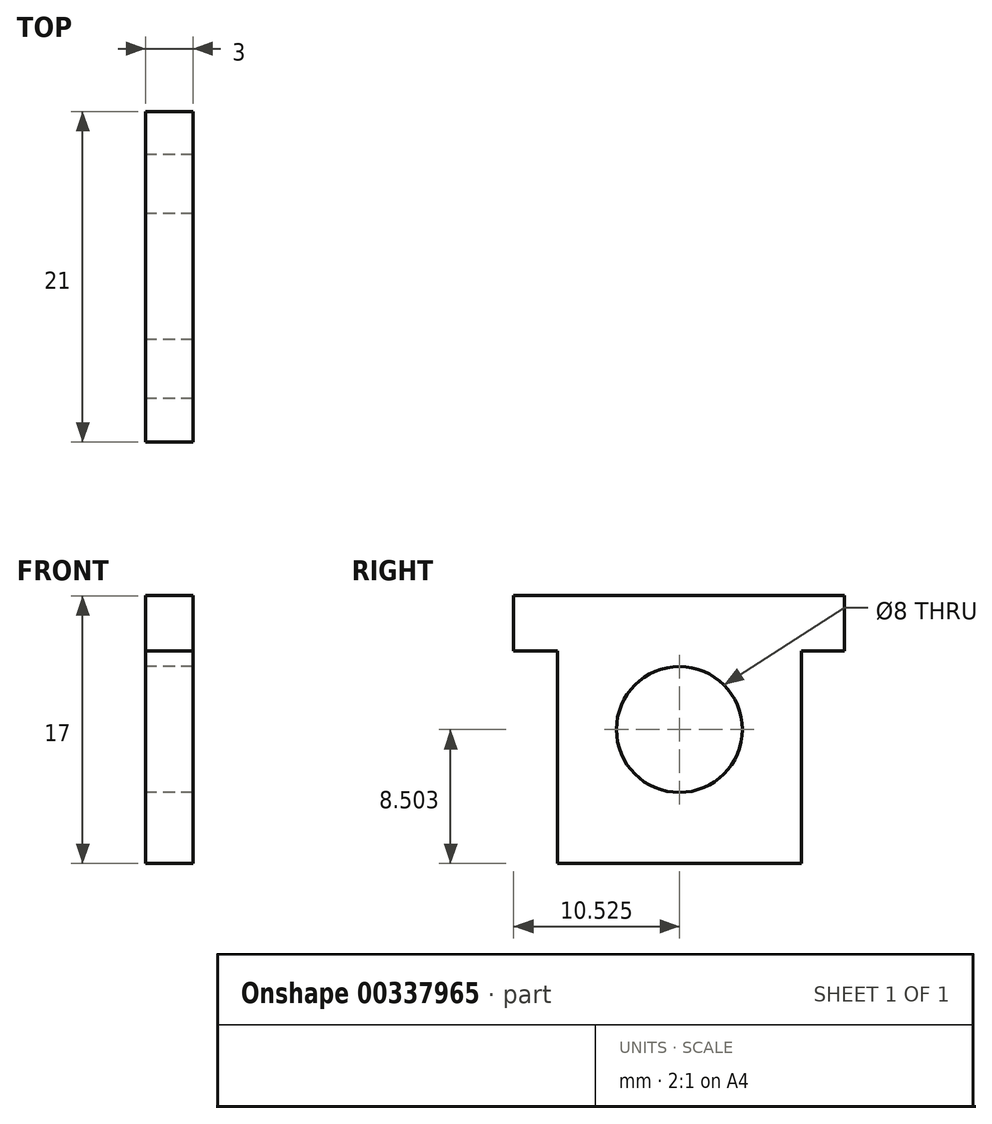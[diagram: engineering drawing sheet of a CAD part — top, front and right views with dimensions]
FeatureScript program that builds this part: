
annotation { "Feature Type Name" : "Feature", "Feature Type Description" : "" }
export const myFeature = defineFeature(function(context is Context, id is Id, definition is map)
    precondition{}
    {
        {
            var Q0;
            Q0=qCreatedBy(makeId("Right.planeOp"),FACE);
            var sketch = newSketch(context, id + "F0", { "sketchPlane" : qUnion([Q0])});
            skLineSegment(sketch, "E0.bottom", {"start": v(-310.36, 146.13) * mm, "end": v(-294.86, 146.13) * mm});
            skLineSegment(sketch, "E0.top", {"start": v(-310.36, 132.63) * mm, "end": v(-294.86, 132.63) * mm});
            skLineSegment(sketch, "E0.left", {"start": v(-310.36, 146.13) * mm, "end": v(-310.36, 132.63) * mm});
            skLineSegment(sketch, "E0.right", {"start": v(-294.86, 146.13) * mm, "end": v(-294.86, 132.63) * mm});
            skPoint(sketch, "E1.oppositeSnap0", {"position": v(-302.6, 146.13) * mm});
            skLineSegment(sketch, "E1.bottom", {"start": v(-313.13, 149.63) * mm, "end": v(-292.13, 149.63) * mm});
            skLineSegment(sketch, "E1.top", {"start": v(-313.13, 146.13) * mm, "end": v(-292.13, 146.13) * mm});
            skLineSegment(sketch, "E1.left", {"start": v(-313.13, 149.63) * mm, "end": v(-313.13, 146.13) * mm});
            skLineSegment(sketch, "E1.right", {"start": v(-292.13, 149.63) * mm, "end": v(-292.13, 146.13) * mm});
            skCircle(sketch, "E2", {"center": v(-302.6, 141.13) * mm, "radius": 4 * mm});
            skSolve(sketch);
        }
        {
            var Q0;
            Q0 = qSketchRegion(id + "F0", true);
            extrude(context, id + "F1", {"entities" : qUnion([Q0]), "depth" : 3 * mm});
        }
    });
